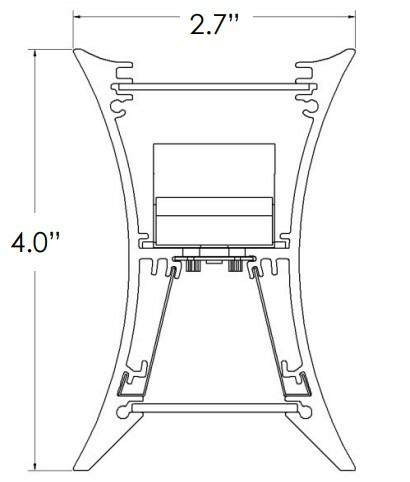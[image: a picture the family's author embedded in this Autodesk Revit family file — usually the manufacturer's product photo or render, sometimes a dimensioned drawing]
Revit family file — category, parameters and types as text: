
# Revit family: 6677888
name_source: partatom
category: Lighting Fixtures
units: mm (PartAtom-declared; Revit-internal decimal feet)

## family parameters
Cut with Voids When Loaded = No
Host = Face
Light Source = Yes
OmniClass Number = 23.80.70.11
OmniClass Title = Luminaries for Internal Lighting
Part Type = Normal
Room Calculation Point = No
Round Connector Dimension = Use Diameter
Shared = No

## types (1)
- Not a type - Load Type Catalog!
    Apparent Load = 0 VA
    Assembly Code = D5020200
    CRI = 80
    Color Filter = 16777215
    Default Elevation = 4' - 0"
    Description = X-Beam Direct/Indirect
    Dimming Lamp Color Temperature Shift = <None>
    Edition number = 1
    Emit Shape Visible in Rendering = No
    Frequency = 60 Hz
    Height = 0' - 4"
    Input Wattage = 0 W
    Keynote = 16500
    Lamp = LED
    Length = 4' - 0"
    Manufacturer = StarTek Lighting
    Number of Poles = 3
    Phase = 1
    Photometric Note = Import IES files https://starteklightingamerica.com
    Photometric Web File = Generic Light Source Shown : Please download and link the IES file that best matches your fixture specification
    Power Factor = 0.93
    Product Guid = b2d46db5-73f3-4843-a0b3-9aa1ceb00019
    Product data url = https://www.bimobject.com
    Type Comments = Linear Lighting Fixture
    URL = https://starteklightingamerica.com
    Voltage = 120 V
    Voltage Range = 120-277V
    Wattage Comments = Efficacy up to 130 lm/W
    Weight = 0.00 lbf
    Width = 0' - 2 1/2"
    z_AC05 = Aircraft Cable : with Canopy 5' (AC05)
    z_AC10 = Aircraft Cable : with Canopy 10' (AC10)
    z_AL10 = Aircraft Cable : with Loops 10' (AL10)
    z_End = Run : End Fixture
    z_Middle = Run : Middle Fixture
    z_Standalone = Run : Standalone Fixture
    z_Start = Run : Start Fixture

## geometry (parser evidence)
native form markers: Sweep x9
no freeform markers — native parametric forms only
